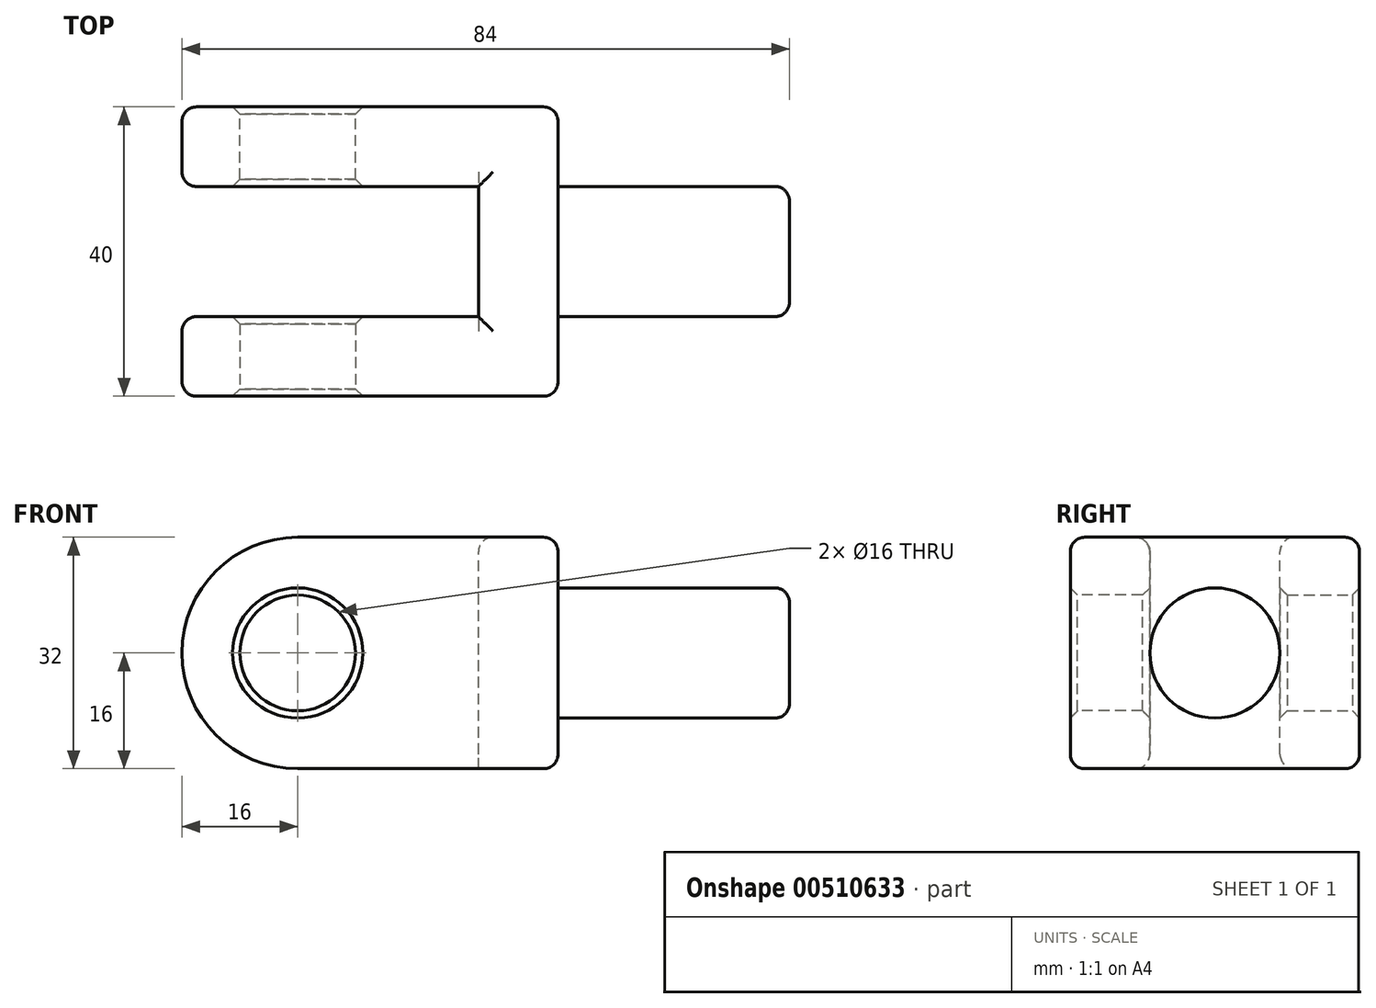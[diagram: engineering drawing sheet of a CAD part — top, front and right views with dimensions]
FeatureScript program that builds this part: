
annotation { "Feature Type Name" : "Feature", "Feature Type Description" : "" }
export const myFeature = defineFeature(function(context is Context, id is Id, definition is map)
    precondition{}
    {
        {
            var Q0;
            Q0=qCreatedBy(makeId("Front.planeOp"),FACE);
            var sketch = newSketch(context, id + "F0", { "sketchPlane" : qUnion([Q0])});
            skLineSegment(sketch, "E0", {"start": v(-11, 0) * mm, "end": v(-11, 32) * mm});
            skLineSegment(sketch, "E1", {"start": v(-11, 32) * mm, "end": v(-36, 32) * mm});
            skLineSegment(sketch, "E2", {"start": v(-11, 0) * mm, "end": v(-36, 0) * mm});
            skLineSegment(sketch, "E3", {"start": v(-11, 32) * mm, "end": v(0, 32) * mm});
            skLineSegment(sketch, "E4", {"start": v(0, 32) * mm, "end": v(0, 0) * mm});
            skLineSegment(sketch, "E5", {"start": v(0, 0) * mm, "end": v(-11, 0) * mm});
            skArc(sketch, "E6", {"start": v(-36, 32) * mm, "mid": v(-52, 16) * mm, "end": v(-36, 0) * mm});
            skCircle(sketch, "E7", {"center": v(-36, 16) * mm, "radius": 8 * mm});
            skSolve(sketch);
        }
        {
            var Q0;
            Q0=makeQuery(id+"F0.imprint","IMPRINT",FACE,{"disambiguationData":[TD([[makeQuery(id+"F0.imprint","IMPRINT",EDGE,{"derivedFrom":sQuery(id+"F0.wireOp",EDGE,"E0")}),1.0]])]});
            extrude(context, id + "F1", {"entities" : qUnion([Q0]), "oppositeDirection" : true, "depth" : 11 * mm});
        }
        {
            var Q0;
            Q0=qCreatedBy(makeId("Front.planeOp"),FACE);
            var sketch = newSketch(context, id + "F2", { "sketchPlane" : qUnion([Q0])});
            skLineSegment(sketch, "E8", {"start": v(-11, 0) * mm, "end": v(0, 0) * mm});
            skLineSegment(sketch, "E9", {"start": v(0, 0) * mm, "end": v(0, 32) * mm});
            skLineSegment(sketch, "E10", {"start": v(0, 32) * mm, "end": v(-11, 32) * mm});
            skLineSegment(sketch, "E11", {"start": v(-11, 32) * mm, "end": v(-11, 0) * mm});
            skSolve(sketch);
        }
        {
            var Q0;
            Q0 = qSketchRegion(id + "F2", true);
            extrude(context, id + "F3", {"entities" : qUnion([Q0]), "operationType" : NewBodyOperationType.ADD, "oppositeDirection" : true, "depth" : 20 * mm});
        }
        {
            var Q0;
            Q0=makeQuery(id+"F1.opExtrude","SWEPT_BODY",BODY,{"disambiguationData":[OSD([sQuery(id+"F0.wireOp",EDGE,"E0"),sQuery(id+"F0.wireOp",EDGE,"E1"),sQuery(id+"F0.wireOp",EDGE,"E2"),sQuery(id+"F0.wireOp",EDGE,"E6"),sQuery(id+"F0.wireOp",EDGE,"E7")])]});
            var Q1;
            Q1=makeQuery(id+"F3.opExtrude","CAP_FACE",FACE,{"disambiguationData":[OSD([sQuery(id+"F2.wireOp",EDGE,"E8"),sQuery(id+"F2.wireOp",EDGE,"E9"),sQuery(id+"F2.wireOp",EDGE,"E10"),sQuery(id+"F2.wireOp",EDGE,"E11")])],"isStart":false});
            mirror(context, id + "F4", {"operationType" : NewBodyOperationType.ADD, "entities" : qUnion([Q0]), "mirrorPlane" : qUnion([Q1])});
        }
        {
            var Q0;
            {var subQ0=makeQuery(id+"F3.opExtrude","SWEPT_FACE",FACE,{"disambiguationData":[OSD([sQuery(id+"F2.wireOp",EDGE,"E9")])]});Q0=makeQuery(id+"F4.boolean.opBoolean","MERGE",FACE,{"derivedFrom":[subQ0,makeQuery(id+"F4.opPattern","COPY",FACE,{"derivedFrom":subQ0,"instanceName":"1"})]});}
            var sketch = newSketch(context, id + "F5", { "sketchPlane" : qUnion([Q0])});
            skCircle(sketch, "E12", {"center": v(20, 16) * mm, "radius": 9 * mm});
            skSolve(sketch);
        }
        {
            var Q0;
            Q0=makeQuery(id+"F5.imprint","IMPRINT",FACE,{"disambiguationData":[TD([[makeQuery(id+"F5.imprint","IMPRINT",EDGE,{"derivedFrom":sQuery(id+"F5.wireOp",EDGE,"E12")}),1.0]])]});
            extrude(context, id + "F6", {"entities" : qUnion([Q0]), "operationType" : NewBodyOperationType.ADD, "depth" : 32 * mm});
        }
        {
            var Q0;
            Q0=makeQuery(id+"F1.opExtrude","CAP_EDGE",EDGE,{"disambiguationData":[OSD([sQuery(id+"F0.wireOp",EDGE,"E7")])],"isStart":true});
            var Q1;
            Q1=makeQuery(id+"F1.opExtrude","CAP_EDGE",EDGE,{"disambiguationData":[OSD([sQuery(id+"F0.wireOp",EDGE,"E7")])],"isStart":false});
            var Q2;
            Q2=makeQuery(id+"F4.opPattern","COPY",EDGE,{"derivedFrom":makeQuery(id+"F1.opExtrude","CAP_EDGE",EDGE,{"disambiguationData":[OSD([sQuery(id+"F0.wireOp",EDGE,"E7")])],"isStart":false}),"instanceName":"1"});
            var Q3;
            Q3=makeQuery(id+"F4.opPattern","COPY",EDGE,{"derivedFrom":makeQuery(id+"F1.opExtrude","CAP_EDGE",EDGE,{"disambiguationData":[OSD([sQuery(id+"F0.wireOp",EDGE,"E7")])],"isStart":true}),"instanceName":"1"});
            chamfer(context, id + "F7", {"entities" : qUnion([Q0, Q1, Q2, Q3]), "width" : 1 * mm, "tangentPropagation" : true});
        }
        {
            var Q0;
            Q0=makeQuery(id+"F6.opExtrude","CAP_EDGE",EDGE,{"disambiguationData":[OSD([sQuery(id+"F5.wireOp",EDGE,"E12")])],"isStart":false});
            var Q1;
            {var subQ0=makeQuery(id+"F3.opExtrude","SWEPT_EDGE",EDGE,{"disambiguationData":[OSD([sQuery(id+"F2.wireOp",EDGE,"E9"),sQuery(id+"F2.wireOp",EDGE,"E10")])]});Q1=makeQuery(id+"F4.boolean.opBoolean","MERGE",EDGE,{"derivedFrom":[subQ0,makeQuery(id+"F4.opPattern","COPY",EDGE,{"derivedFrom":subQ0,"instanceName":"1"})]});}
            var Q2;
            Q2=makeQuery(id+"F4.opPattern","COPY",EDGE,{"derivedFrom":makeQuery(id+"F3.opExtrude","CAP_EDGE",EDGE,{"disambiguationData":[OSD([sQuery(id+"F2.wireOp",EDGE,"E9")])],"isStart":true}),"instanceName":"1"});
            var Q3;
            {var subQ0=makeQuery(id+"F3.opExtrude","SWEPT_EDGE",EDGE,{"disambiguationData":[OSD([sQuery(id+"F2.wireOp",EDGE,"E8"),sQuery(id+"F2.wireOp",EDGE,"E9")])]});Q3=makeQuery(id+"F4.boolean.opBoolean","MERGE",EDGE,{"derivedFrom":[subQ0,makeQuery(id+"F4.opPattern","COPY",EDGE,{"derivedFrom":subQ0,"instanceName":"1"})]});}
            var Q4;
            Q4=makeQuery(id+"F3.opExtrude","CAP_EDGE",EDGE,{"disambiguationData":[OSD([sQuery(id+"F2.wireOp",EDGE,"E9")])],"isStart":true});
            var Q5;
            {var subQ0=makeQuery(id+"F3.boolean.opBoolean","MERGE",FACE,{"derivedFrom":[makeQuery(id+"F1.opExtrude","SWEPT_FACE",FACE,{"disambiguationData":[OSD([sQuery(id+"F0.wireOp",EDGE,"E1")])]}),makeQuery(id+"F3.opExtrude","SWEPT_FACE",FACE,{"disambiguationData":[OSD([sQuery(id+"F2.wireOp",EDGE,"E10")])]})]});Q5=makeQuery(id+"F4.boolean.opBoolean","MERGE",FACE,{"derivedFrom":[subQ0,makeQuery(id+"F4.opPattern","COPY",FACE,{"derivedFrom":subQ0,"instanceName":"1"})]});}
            fillet(context, id + "F8", {"entities" : qUnion([Q0, Q1, Q2, Q3, Q4, Q5]), "radius" : 2 * mm, "tangentPropagation" : true, "allowEdgeOverflow" : false});
        }
    });
